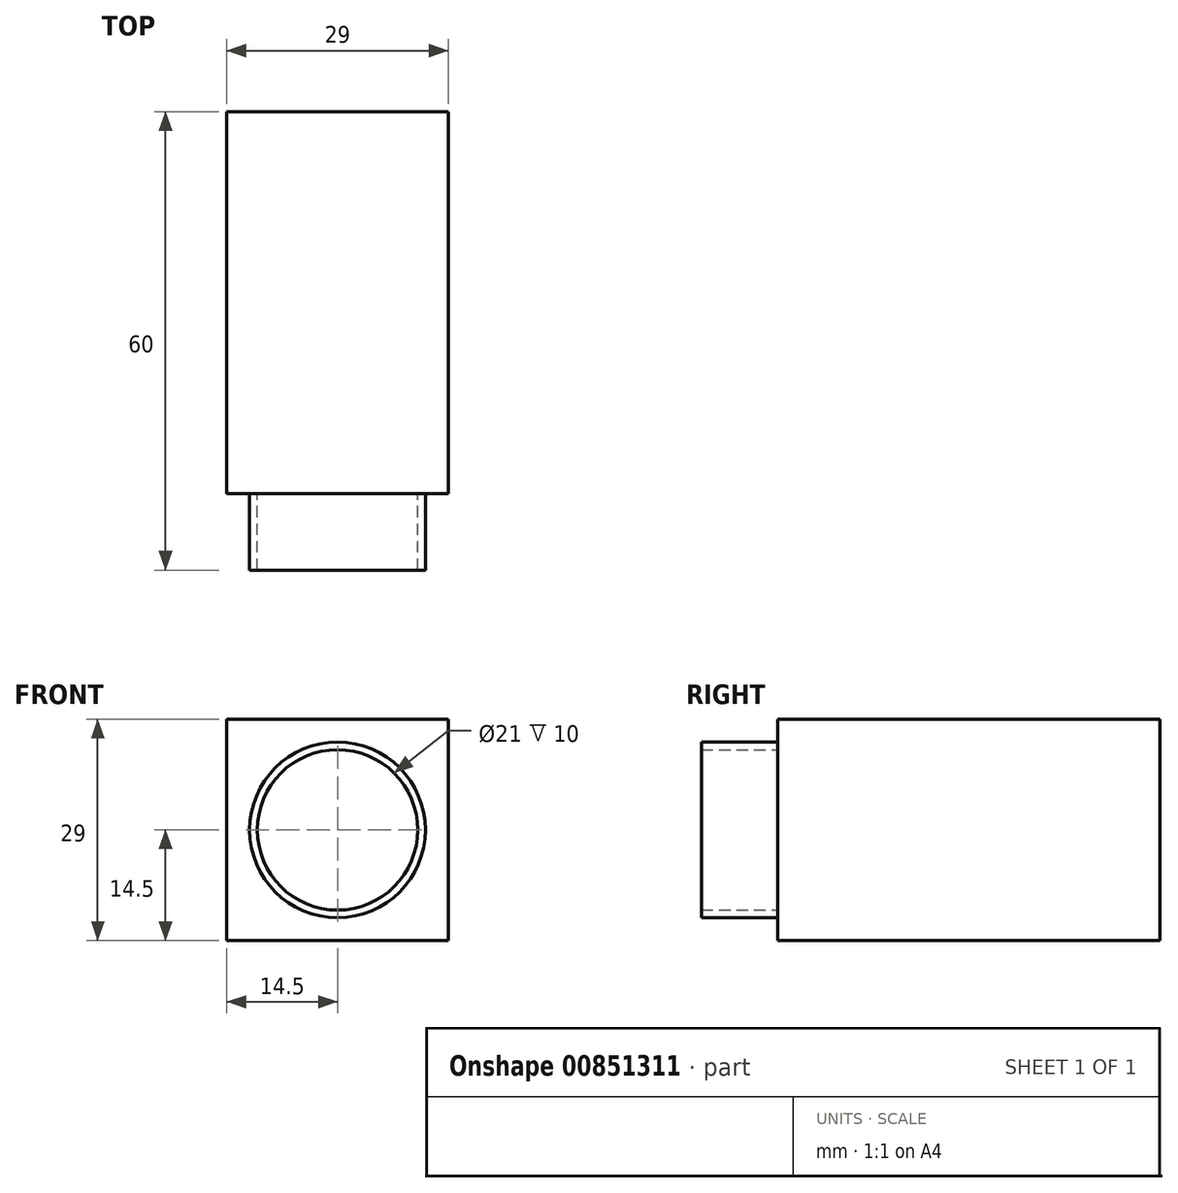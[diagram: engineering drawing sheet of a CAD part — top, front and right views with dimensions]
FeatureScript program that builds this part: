
annotation { "Feature Type Name" : "Feature", "Feature Type Description" : "" }
export const myFeature = defineFeature(function(context is Context, id is Id, definition is map)
    precondition{}
    {
        {
            var Q0;
            Q0=qCreatedBy(makeId("Front.planeOp"),FACE);
            var sketch = newSketch(context, id + "F0", { "sketchPlane" : qUnion([Q0])});
            skLineSegment(sketch, "E0.bottom", {"start": v(14.5, 14.5) * mm, "end": v(-14.5, 14.5) * mm});
            skLineSegment(sketch, "E0.top", {"start": v(14.5, -14.5) * mm, "end": v(-14.5, -14.5) * mm});
            skLineSegment(sketch, "E0.left", {"start": v(14.5, 14.5) * mm, "end": v(14.5, -14.5) * mm});
            skLineSegment(sketch, "E0.right", {"start": v(-14.5, 14.5) * mm, "end": v(-14.5, -14.5) * mm});
            skPoint(sketch, "E0.middle", {"position": v(0, 0) * mm});
            skSolve(sketch);
        }
        {
            var Q0;
            Q0 = qSketchRegion(id + "F0", true);
            extrude(context, id + "F1", {"entities" : qUnion([Q0]), "depth" : 50 * mm, "offsetDistance" : 25 * mm});
        }
        {
            var Q0;
            Q0=makeQuery(id+"F1.opExtrude","CAP_FACE",FACE,{"disambiguationData":[OSD([sQuery(id+"F0.wireOp",EDGE,"E0.bottom"),sQuery(id+"F0.wireOp",EDGE,"E0.top"),sQuery(id+"F0.wireOp",EDGE,"E0.left"),sQuery(id+"F0.wireOp",EDGE,"E0.right")])],"isStart":false});
            var sketch = newSketch(context, id + "F2", { "sketchPlane" : qUnion([Q0])});
            skCircle(sketch, "E1", {"center": v(0, 0) * mm, "radius": 11.5 * mm});
            skCircle(sketch, "E2", {"center": v(0, 0) * mm, "radius": 10.5 * mm});
            skSolve(sketch);
        }
        {
            var Q0;
            Q0 = qSketchRegion(id + "F2", true);
            extrude(context, id + "F3", {"entities" : qUnion([Q0]), "operationType" : NewBodyOperationType.ADD, "depth" : 10 * mm, "offsetDistance" : 25 * mm});
        }
    });
